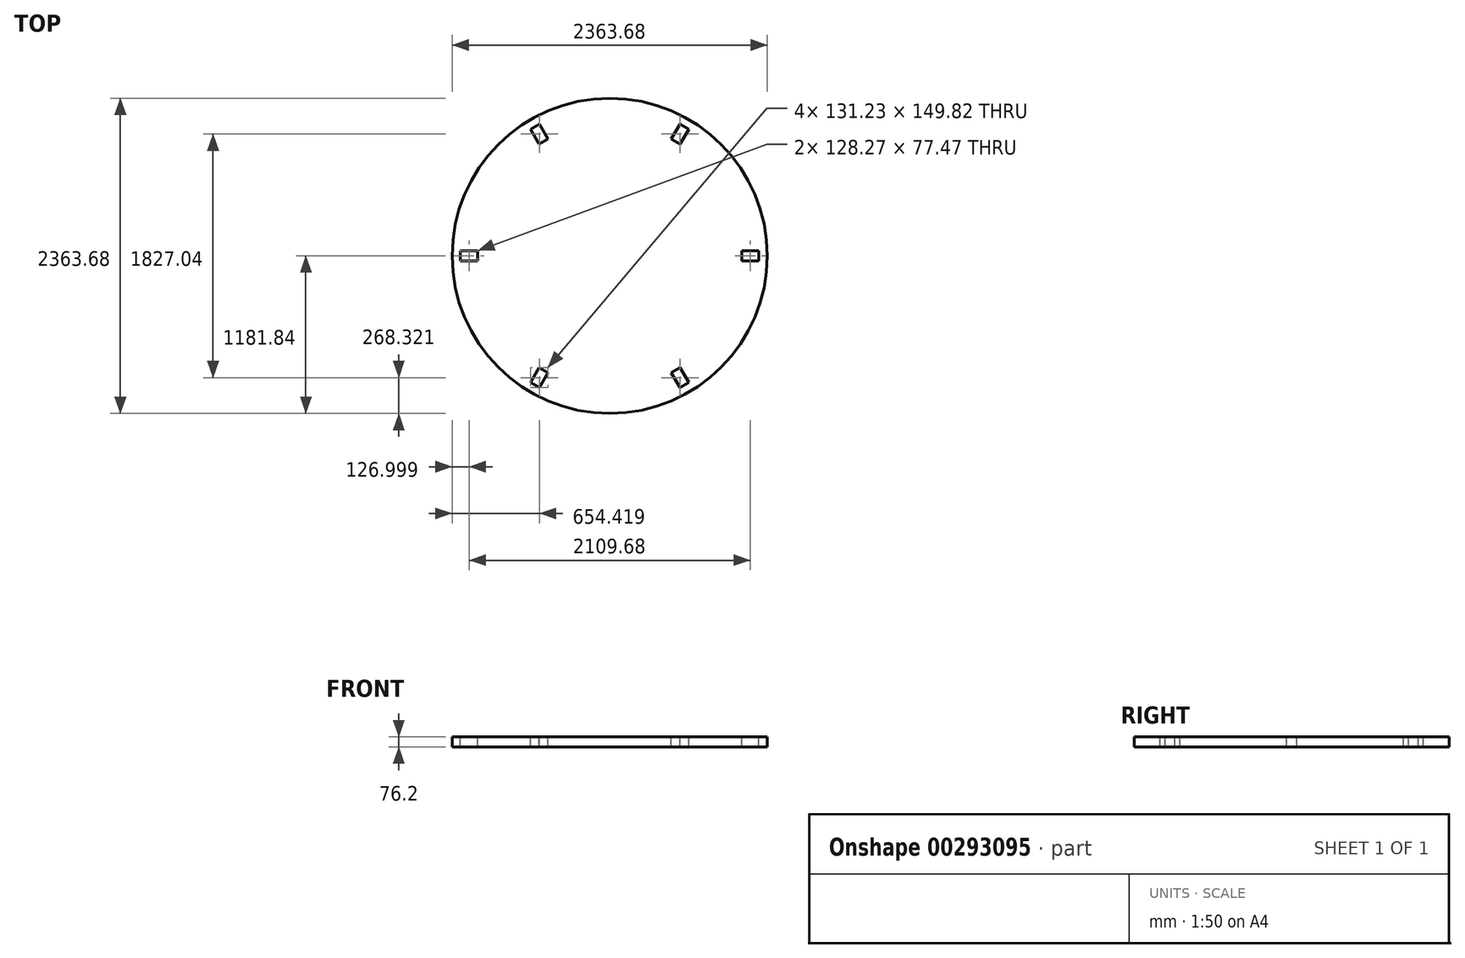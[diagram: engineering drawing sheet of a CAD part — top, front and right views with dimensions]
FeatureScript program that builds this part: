
annotation { "Feature Type Name" : "Feature", "Feature Type Description" : "" }
export const myFeature = defineFeature(function(context is Context, id is Id, definition is map)
    precondition{}
    {
        {
            var Q0;
            Q0=qCreatedBy(makeId("Front.planeOp"),FACE);
            var sketch = newSketch(context, id + "F0", { "sketchPlane" : qUnion([Q0])});
            skLineSegment(sketch, "E0", {"start": v(-1181.84, -1151.07) * mm, "end": v(-927.84, -1151.07) * mm});
            skFitSpline(sketch, "E1", {"points": [v(0, 1953.18) * mm, v(-1100.72, 1005.66) * mm, v(-1321.31, -446.19) * mm, v(-1216.83, -971.83) * mm, v(-1181.84, -1151.07) * mm], "startDerivative": vector(-4000.43, 5.06) * mm, "endDerivative": vector(0, -1489.55) * mm});
            skLineSegment(sketch, "E2", {"start": v(-1099.69, 1007.93) * mm, "end": v(-930.94, 1007.93) * mm});
            skLineSegment(sketch, "E3", {"start": v(-1181.84, -1151.07) * mm, "end": v(-1181.84, -1354.27) * mm});
            skLineSegment(sketch, "E4", {"start": v(-1181.84, -1354.27) * mm, "end": v(-877.04, -1354.27) * mm});
            skLineSegment(sketch, "E5", {"start": v(-877.04, -1354.27) * mm, "end": v(-877.04, -1252.67) * mm});
            skLineSegment(sketch, "E6", {"start": v(-877.04, -1252.67) * mm, "end": v(-927.84, -1252.67) * mm});
            skLineSegment(sketch, "E7", {"start": v(-927.84, -1252.67) * mm, "end": v(-927.84, -1151.07) * mm});
            skFitSpline(sketch, "E8.trimOffspring", {"points": [v(0, -1758.08) * mm, v(-927.84, -1151.07) * mm, v(-1179.31, -127.97) * mm, v(-917.89, 1033.92) * mm, v(0, 1800.5) * mm], "startDerivative": vector(-4973.2, 113.59) * mm, "endDerivative": vector(4756.7, 336.76) * mm});
            skLineSegment(sketch, "E9", {"start": v(-1023.33, 1160.33) * mm, "end": v(-848.12, 1160.33) * mm});
            skLineSegment(sketch, "E10", {"start": v(0, 1953.18) * mm, "end": v(0, 1800.5) * mm});
            skLineSegment(sketch, "E11.bottom", {"start": v(-1118.34, -1074.87) * mm, "end": v(-991.34, -1074.87) * mm});
            skLineSegment(sketch, "E11.top", {"start": v(-1118.34, -1227.27) * mm, "end": v(-991.34, -1227.27) * mm});
            skLineSegment(sketch, "E11.left", {"start": v(-1118.34, -1074.87) * mm, "end": v(-1118.34, -1227.27) * mm});
            skLineSegment(sketch, "E11.right", {"start": v(-991.34, -1074.87) * mm, "end": v(-991.34, -1227.27) * mm});
            skPoint(sketch, "E11.middle", {"position": v(-1054.84, -1151.07) * mm});
            skLineSegment(sketch, "E12.bottom", {"start": v(-1053.41, 1084.13) * mm, "end": v(-977.21, 1084.13) * mm});
            skLineSegment(sketch, "E12.top", {"start": v(-1053.41, 931.73) * mm, "end": v(-977.21, 931.73) * mm});
            skLineSegment(sketch, "E12.left", {"start": v(-1053.41, 1084.13) * mm, "end": v(-1053.41, 931.73) * mm});
            skLineSegment(sketch, "E12.right", {"start": v(-977.21, 1084.13) * mm, "end": v(-977.21, 931.73) * mm});
            skPoint(sketch, "E12.middle", {"position": v(-1015.31, 1007.93) * mm});
            skLineSegment(sketch, "E13", {"start": v(-891.46, 1084.13) * mm, "end": v(-1063.3, 1084.13) * mm});
            skLineSegment(sketch, "E14", {"start": v(-889.38, 1087.96) * mm, "end": v(-1061.37, 1087.96) * mm});
            skLineSegment(sketch, "E15", {"start": v(-76.2, 1949.03) * mm, "end": v(-76.2, 1791.14) * mm});
            skLineSegment(sketch, "E16", {"start": v(-76.2, 1791.14) * mm, "end": v(-76.2, 1796.63) * mm});
            skLineSegment(sketch, "E17", {"start": v(-76.2, 1796.63) * mm, "end": v(-127, 1796.63) * mm});
            skLineSegment(sketch, "E18", {"start": v(-127, 1796.63) * mm, "end": v(-127, 1872.83) * mm});
            skLineSegment(sketch, "E19", {"start": v(-127, 1872.83) * mm, "end": v(-76.2, 1872.83) * mm});
            skLineSegment(sketch, "E20", {"start": v(-889.38, 1087.96) * mm, "end": v(-810.8, 1087.96) * mm});
            skLineSegment(sketch, "E21", {"start": v(-810.8, 1087.96) * mm, "end": v(-680.59, 1399.26) * mm});
            skLineSegment(sketch, "E22", {"start": v(-810.8, 1087.96) * mm, "end": v(-810.8, 1004.5) * mm});
            skLineSegment(sketch, "E23", {"start": v(-889.38, 1087.96) * mm, "end": v(-889.38, 1004.5) * mm});
            skLineSegment(sketch, "E24", {"start": v(-889.38, 1004.5) * mm, "end": v(-810.8, 1004.5) * mm});
            skFitSpline(sketch, "E25", {"points": [v(-554.31, 1534.3) * mm, v(-76.2, 1720.43) * mm], "startDerivative": vector(464.08, 398.04) * mm, "endDerivative": vector(465.1, 29.66) * mm});
            skLineSegment(sketch, "E26", {"start": v(-76.2, 1720.43) * mm, "end": v(-76.2, 1791.14) * mm});
            skLineSegment(sketch, "E27", {"start": v(-930.94, 1007.93) * mm, "end": v(-927.84, -1151.07) * mm});
            skSolve(sketch);
        }
        {
            var Q0;
            Q0=qCreatedBy(makeId("Top.planeOp"),FACE);
            var Q1;
            Q1=sQuery(id+"F0.wireOp",VERTEX,"E8.trimOffspring.1.internal");
            cPlane(context, id + "F1", {"entities" : qUnion([Q0, Q1]), "cplaneType" : CPlaneType.PLANE_POINT, "offset" : 25.4 * mm, "width" : 152.4 * mm, "height" : 152.4 * mm});
        }
        {
            var Q0;
            Q0=qCreatedBy(id+"F1.planeOp",FACE);
            var sketch = newSketch(context, id + "F2", { "sketchPlane" : qUnion([Q0])});
            skCircle(sketch, "E28", {"center": v(0, 0) * mm, "radius": 1181.84 * mm});
            skLineSegment(sketch, "E29.bottom", {"start": v(-1118.98, 38.73) * mm, "end": v(-990.7, 38.73) * mm});
            skLineSegment(sketch, "E29.top", {"start": v(-1118.98, -38.74) * mm, "end": v(-990.7, -38.74) * mm});
            skLineSegment(sketch, "E29.left", {"start": v(-1118.98, 38.73) * mm, "end": v(-1118.98, -38.74) * mm});
            skLineSegment(sketch, "E29.right", {"start": v(-990.7, 38.73) * mm, "end": v(-990.7, -38.74) * mm});
            skPoint(sketch, "E29.middle", {"position": v(-1054.84, 0) * mm});
            skLineSegment(sketch, "E30.1.0", {"start": v(-593.03, -949.7) * mm, "end": v(-528.9, -838.6) * mm});
            skLineSegment(sketch, "E30.1.1", {"start": v(-593.03, -949.7) * mm, "end": v(-525.94, -988.43) * mm});
            skLineSegment(sketch, "E30.1.2", {"start": v(-525.94, -988.43) * mm, "end": v(-461.8, -877.34) * mm});
            skLineSegment(sketch, "E30.1.3", {"start": v(-528.9, -838.6) * mm, "end": v(-461.8, -877.34) * mm});
            skLineSegment(sketch, "E30.2.0", {"start": v(525.94, -988.43) * mm, "end": v(461.8, -877.34) * mm});
            skLineSegment(sketch, "E30.2.1", {"start": v(525.94, -988.43) * mm, "end": v(593.03, -949.7) * mm});
            skLineSegment(sketch, "E30.2.2", {"start": v(593.03, -949.7) * mm, "end": v(528.9, -838.6) * mm});
            skLineSegment(sketch, "E30.2.3", {"start": v(461.8, -877.34) * mm, "end": v(528.9, -838.6) * mm});
            skLineSegment(sketch, "E30.3.0", {"start": v(1118.98, -38.74) * mm, "end": v(990.7, -38.74) * mm});
            skLineSegment(sketch, "E30.3.1", {"start": v(1118.98, -38.74) * mm, "end": v(1118.98, 38.73) * mm});
            skLineSegment(sketch, "E30.3.2", {"start": v(1118.98, 38.73) * mm, "end": v(990.7, 38.73) * mm});
            skLineSegment(sketch, "E30.3.3", {"start": v(990.7, -38.74) * mm, "end": v(990.7, 38.73) * mm});
            skLineSegment(sketch, "E30.4.0", {"start": v(593.03, 949.7) * mm, "end": v(528.9, 838.6) * mm});
            skLineSegment(sketch, "E30.4.1", {"start": v(593.03, 949.7) * mm, "end": v(525.94, 988.43) * mm});
            skLineSegment(sketch, "E30.4.2", {"start": v(525.94, 988.43) * mm, "end": v(461.8, 877.34) * mm});
            skLineSegment(sketch, "E30.4.3", {"start": v(528.9, 838.6) * mm, "end": v(461.8, 877.34) * mm});
            skLineSegment(sketch, "E30.5.0", {"start": v(-525.94, 988.43) * mm, "end": v(-461.8, 877.34) * mm});
            skLineSegment(sketch, "E30.5.1", {"start": v(-525.94, 988.43) * mm, "end": v(-593.03, 949.7) * mm});
            skLineSegment(sketch, "E30.5.2", {"start": v(-593.03, 949.7) * mm, "end": v(-528.9, 838.6) * mm});
            skLineSegment(sketch, "E30.5.3", {"start": v(-461.8, 877.34) * mm, "end": v(-528.9, 838.6) * mm});
            skSolve(sketch);
        }
        {
            var Q0;
            Q0=makeQuery(id+"F2.imprint","IMPRINT",FACE,{"disambiguationData":[TD([[makeQuery(id+"F2.imprint","IMPRINT",EDGE,{"derivedFrom":sQuery(id+"F2.wireOp",EDGE,"E28")}),1.0]])]});
            extrude(context, id + "F3", {"entities" : qUnion([Q0]), "oppositeDirection" : true, "depth" : 76.2 * mm});
        }
        {
            var Q0;
            Q0=qCreatedBy(makeId("Top.planeOp"),FACE);
            var Q1;
            Q1=sQuery(id+"F0.wireOp",VERTEX,"E2.end");
            cPlane(context, id + "F4", {"entities" : qUnion([Q0, Q1]), "cplaneType" : CPlaneType.PLANE_POINT, "offset" : 25.4 * mm, "width" : 152.4 * mm, "height" : 152.4 * mm});
        }
    });
